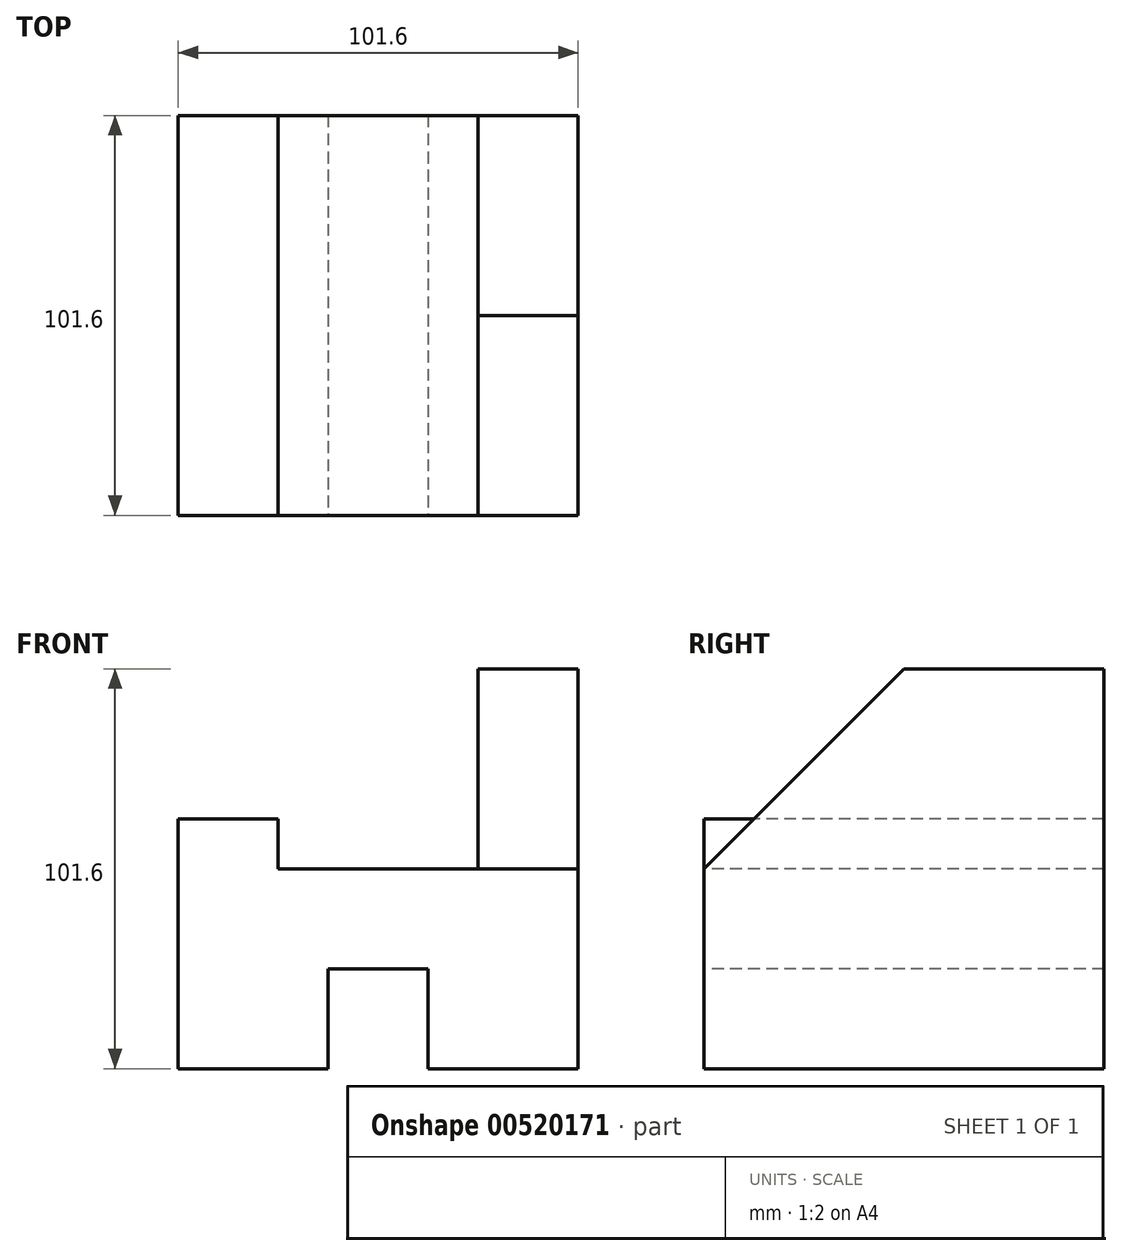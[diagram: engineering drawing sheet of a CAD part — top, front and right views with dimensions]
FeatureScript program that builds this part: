
annotation { "Feature Type Name" : "Feature", "Feature Type Description" : "" }
export const myFeature = defineFeature(function(context is Context, id is Id, definition is map)
    precondition{}
    {
        {
            var Q0;
            Q0=qCreatedBy(makeId("Front.planeOp"),FACE);
            var sketch = newSketch(context, id + "F0", { "sketchPlane" : qUnion([Q0])});
            skLineSegment(sketch, "E0.bottom", {"start": v(-39.82, -60.1) * mm, "end": v(61.78, -60.1) * mm});
            skLineSegment(sketch, "E0.top", {"start": v(-39.82, 41.5) * mm, "end": v(61.78, 41.5) * mm});
            skLineSegment(sketch, "E0.left", {"start": v(-39.82, -60.1) * mm, "end": v(-39.82, 41.5) * mm});
            skLineSegment(sketch, "E0.right", {"start": v(61.78, -60.1) * mm, "end": v(61.78, 41.5) * mm});
            skSolve(sketch);
        }
        {
            var Q0;
            Q0=makeQuery(id+"F0.imprint","IMPRINT",FACE,{"disambiguationData":[TD([[makeQuery(id+"F0.imprint","IMPRINT",EDGE,{"derivedFrom":sQuery(id+"F0.wireOp",EDGE,"E0.bottom")}),1.0]])]});
            extrude(context, id + "F1", {"entities" : qUnion([Q0]), "depth" : 101.6 * mm, "offsetDistance" : 25.4 * mm});
        }
        {
            var Q0;
            Q0=makeQuery(id+"F1.opExtrude","CAP_FACE",FACE,{"disambiguationData":[OSD([sQuery(id+"F0.wireOp",EDGE,"E0.bottom"),sQuery(id+"F0.wireOp",EDGE,"E0.top"),sQuery(id+"F0.wireOp",EDGE,"E0.left"),sQuery(id+"F0.wireOp",EDGE,"E0.right")])],"isStart":false});
            var sketch = newSketch(context, id + "F2", { "sketchPlane" : qUnion([Q0])});
            skLineSegment(sketch, "E1", {"start": v(-39.82, 3.4) * mm, "end": v(-14.42, 3.4) * mm});
            skLineSegment(sketch, "E2", {"start": v(-14.42, 3.4) * mm, "end": v(-14.42, -9.3) * mm});
            skLineSegment(sketch, "E3", {"start": v(-14.42, -9.3) * mm, "end": v(36.38, -9.3) * mm});
            skLineSegment(sketch, "E4", {"start": v(36.38, -9.3) * mm, "end": v(36.38, 41.5) * mm});
            skLineSegment(sketch, "E5", {"start": v(-1.72, -60.1) * mm, "end": v(23.68, -60.1) * mm});
            skLineSegment(sketch, "E6", {"start": v(23.68, -60.1) * mm, "end": v(61.78, -60.1) * mm});
            skSolve(sketch);
        }
        {
            var Q0;
            Q0 = qSketchRegion(id + "F2", true);
            var Q1;
            {var subQ1=sQuery(id+"F2.wireOp",EDGE,"E1");Q1=makeQuery(id+"F2.imprint","IMPRINT",FACE,{"disambiguationData":[TD([[makeQuery(id+"F2.imprint","IMPRINT",EDGE,{"derivedFrom":subQ1}),1.0]])]});}
            extrude(context, id + "F3", {"entities" : qUnion([Q0, Q1]), "operationType" : NewBodyOperationType.REMOVE, "oppositeDirection" : true, "depth" : 101.6 * mm, "offsetDistance" : 25.4 * mm});
        }
        {
            var Q0;
            Q0=makeQuery(id+"F1.opExtrude","CAP_FACE",FACE,{"disambiguationData":[OSD([sQuery(id+"F0.wireOp",EDGE,"E0.bottom"),sQuery(id+"F0.wireOp",EDGE,"E0.top"),sQuery(id+"F0.wireOp",EDGE,"E0.left"),sQuery(id+"F0.wireOp",EDGE,"E0.right")])],"isStart":false});
            var sketch = newSketch(context, id + "F4", { "sketchPlane" : qUnion([Q0])});
            skLineSegment(sketch, "E7", {"start": v(-1.72, -60.1) * mm, "end": v(23.68, -60.1) * mm});
            skLineSegment(sketch, "E8", {"start": v(-1.72, -60.1) * mm, "end": v(-1.72, -34.7) * mm});
            skLineSegment(sketch, "E9", {"start": v(-1.72, -34.7) * mm, "end": v(23.68, -34.7) * mm});
            skLineSegment(sketch, "E10", {"start": v(23.68, -34.7) * mm, "end": v(23.68, -60.1) * mm});
            skSolve(sketch);
        }
        {
            var Q0;
            Q0 = qSketchRegion(id + "F4", true);
            extrude(context, id + "F5", {"entities" : qUnion([Q0]), "operationType" : NewBodyOperationType.REMOVE, "oppositeDirection" : true, "depth" : 101.6 * mm, "offsetDistance" : 25.4 * mm});
        }
        {
            var Q0;
            Q0=makeQuery(id+"F1.opExtrude","SWEPT_FACE",FACE,{"disambiguationData":[OSD([sQuery(id+"F0.wireOp",EDGE,"E0.right")])]});
            var sketch = newSketch(context, id + "F6", { "sketchPlane" : qUnion([Q0])});
            skLineSegment(sketch, "E11", {"start": v(-50.8, 41.5) * mm, "end": v(-101.6, -9.3) * mm});
            skSolve(sketch);
        }
        {
            var Q0;
            {var subQ0=sQuery(id+"F6.wireOp",EDGE,"E11");Q0=makeQuery(id+"F6.imprint","IMPRINT",FACE,{"disambiguationData":[TD([[makeQuery(id+"F6.imprint","IMPRINT",EDGE,{"derivedFrom":subQ0}),-1.0]])]});}
            extrude(context, id + "F7", {"entities" : qUnion([Q0]), "operationType" : NewBodyOperationType.REMOVE, "oppositeDirection" : true, "depth" : 25.4 * mm, "offsetDistance" : 25.4 * mm});
        }
    });
